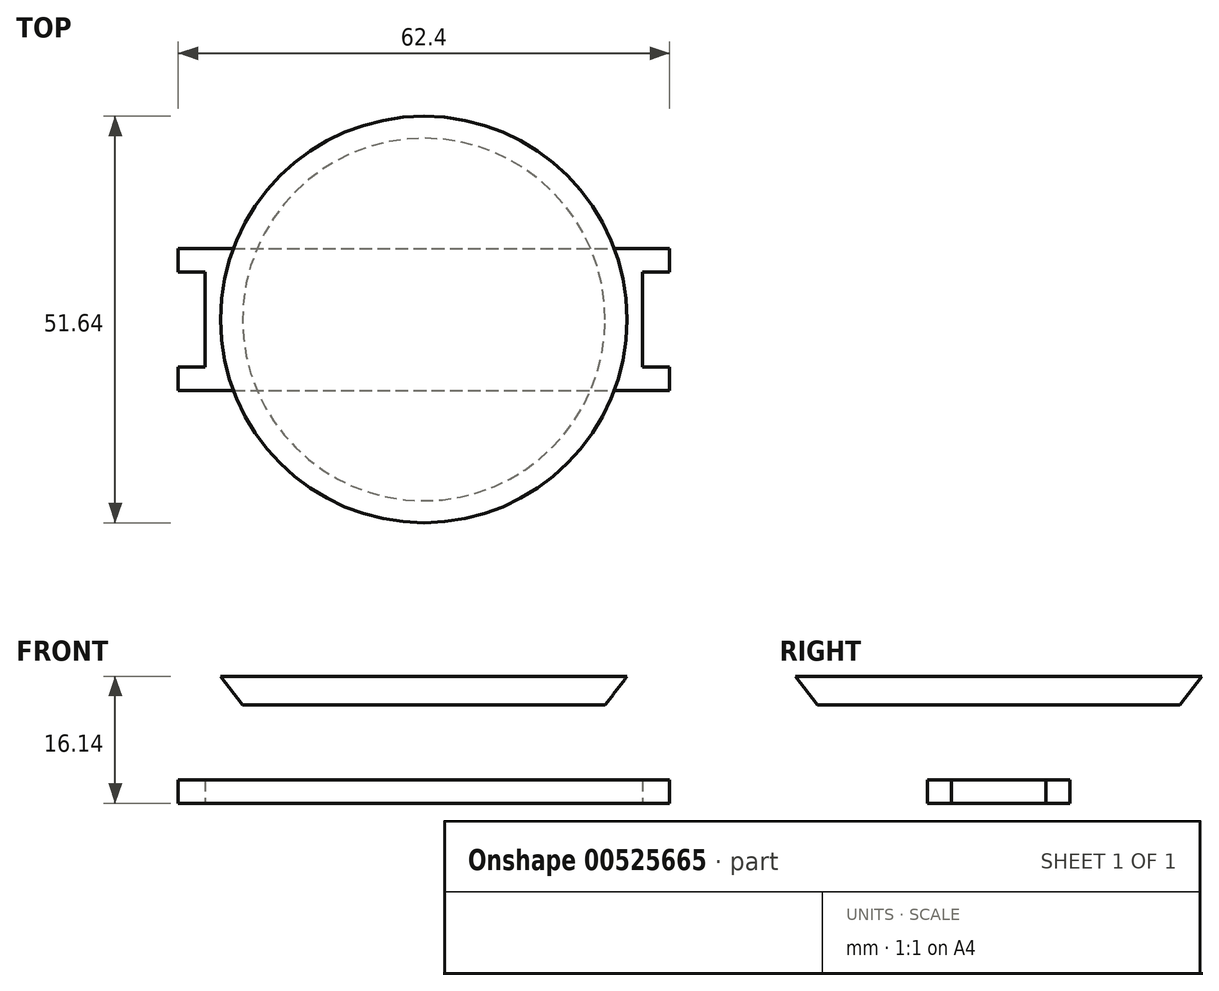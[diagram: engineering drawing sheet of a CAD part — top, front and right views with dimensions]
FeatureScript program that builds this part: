
annotation { "Feature Type Name" : "Feature", "Feature Type Description" : "" }
export const myFeature = defineFeature(function(context is Context, id is Id, definition is map)
    precondition{}
    {
        {
            var Q0;
            Q0=qCreatedBy(makeId("Front.planeOp"),FACE);
            var sketch = newSketch(context, id + "F0", { "sketchPlane" : qUnion([Q0])});
            skLineSegment(sketch, "E0", {"start": v(0, 12.48) * mm, "end": v(23.02, 12.48) * mm});
            skLineSegment(sketch, "E1", {"start": v(23.02, 12.48) * mm, "end": v(25.82, 16.14) * mm});
            skLineSegment(sketch, "E2", {"start": v(25.82, 16.14) * mm, "end": v(0, 16.14) * mm});
            skLineSegment(sketch, "E3", {"start": v(0, 16.14) * mm, "end": v(0, 12.48) * mm});
            skSolve(sketch);
        }
        {
            var Q0;
            Q0=makeQuery(id+"F0.imprint","IMPRINT",FACE,{"disambiguationData":[TD([[makeQuery(id+"F0.imprint","IMPRINT",EDGE,{"derivedFrom":sQuery(id+"F0.wireOp",EDGE,"E0")}),1.0]])]});
            var Q1;
            Q1=sQuery(id+"F0.wireOp",EDGE,"E3");
            revolve(context, id + "F1", {"entities" : qUnion([Q0]), "axis" : qUnion([Q1]), "revolveType" : RevolveType.FULL});
        }
        {
            var Q0;
            Q0=qCreatedBy(makeId("Top.planeOp"),FACE);
            var sketch = newSketch(context, id + "F2", { "sketchPlane" : qUnion([Q0])});
            skLineSegment(sketch, "E4", {"start": v(0, -9.04) * mm, "end": v(31.2, -9.04) * mm});
            skLineSegment(sketch, "E5", {"start": v(31.2, -9.04) * mm, "end": v(31.2, -6.02) * mm});
            skLineSegment(sketch, "E6", {"start": v(31.2, -6.02) * mm, "end": v(27.76, -6.02) * mm});
            skLineSegment(sketch, "E7", {"start": v(27.76, -6.02) * mm, "end": v(27.76, 0) * mm});
            skLineSegment(sketch, "E8", {"start": v(27.76, 0) * mm, "end": v(0, 0) * mm});
            skLineSegment(sketch, "E9", {"start": v(0, 0) * mm, "end": v(0, -9.04) * mm});
            skLineSegment(sketch, "E10.MirrorCS", {"start": v(-31.2, -6.02) * mm, "end": v(-27.76, -6.02) * mm});
            skLineSegment(sketch, "E11.MirrorCS", {"start": v(-27.76, 0) * mm, "end": v(0, 0) * mm});
            skLineSegment(sketch, "E12.MirrorCS", {"start": v(-27.76, -6.02) * mm, "end": v(-27.76, 0) * mm});
            skLineSegment(sketch, "E13.MirrorCS", {"start": v(-31.2, -9.04) * mm, "end": v(-31.2, -6.02) * mm});
            skLineSegment(sketch, "E14.MirrorCS", {"start": v(0, -9.04) * mm, "end": v(-31.2, -9.04) * mm});
            skLineSegment(sketch, "E15.MirrorCS", {"start": v(-31.2, 6.02) * mm, "end": v(-27.76, 6.02) * mm});
            skLineSegment(sketch, "E16.MirrorCS", {"start": v(0, 0) * mm, "end": v(0, 9.04) * mm});
            skLineSegment(sketch, "E17.MirrorCS", {"start": v(27.76, 6.02) * mm, "end": v(27.76, 0) * mm});
            skLineSegment(sketch, "E18.MirrorCS", {"start": v(31.2, 6.02) * mm, "end": v(27.76, 6.02) * mm});
            skLineSegment(sketch, "E19.MirrorCS", {"start": v(31.2, 9.04) * mm, "end": v(31.2, 6.02) * mm});
            skLineSegment(sketch, "E20.MirrorCS", {"start": v(0, 9.04) * mm, "end": v(31.2, 9.04) * mm});
            skLineSegment(sketch, "E21.MirrorCS", {"start": v(0, 9.04) * mm, "end": v(-31.2, 9.04) * mm});
            skLineSegment(sketch, "E22.MirrorCS", {"start": v(-27.76, 6.02) * mm, "end": v(-27.76, 0) * mm});
            skLineSegment(sketch, "E23.MirrorCS", {"start": v(-31.2, 9.04) * mm, "end": v(-31.2, 6.02) * mm});
            skSolve(sketch);
        }
        {
            var Q0;
            Q0 = qSketchRegion(id + "F2", true);
            extrude(context, id + "F3", {"entities" : qUnion([Q0]), "depth" : 3 * mm, "offsetDistance" : 25 * mm});
        }
    });
